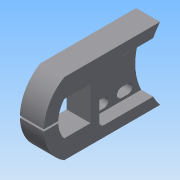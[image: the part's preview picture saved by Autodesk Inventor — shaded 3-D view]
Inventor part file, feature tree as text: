
AUTODESK INVENTOR PART (.ipt)
format: ipt  version: 2015 (Build 190159000, 159)  size: 153,600 bytes
history: native  units: in
note: dims shown in document units (in); Inventor stores cm internally (conversion verified against a paired STEP export)
features: extrude x2, sketch x2
ambient origin geometry x8: Origin, YZ Plane, XZ Plane, XY Plane, X Axis, Y Axis, Z Axis, Center Point
bodies: Solid1 (feature_tree)
feature tree (4):
  extrude  "Extrusion1"  Depth=0.71in
  extrude  "Extrusion2"  Depth=1.1811in
  sketch  "Sketch1"  dims[d0=0.55in d1=0.71in]
  sketch  "Sketch2"  dims[d2=0.1in d4=1.1811in d8=0.196in d9=0.098in d17=0.125in d18=0.7874in d20=0.5in d21=0.7874in d23=0.75in d26=1.5in d30=0.4in d31=0.3in d32=2.6394in d33=0.0394in d34=0.5in d35=0.0in d37=1.0in d38=1.125in d39=0.098in d40=0.25in d41=0.0in]
